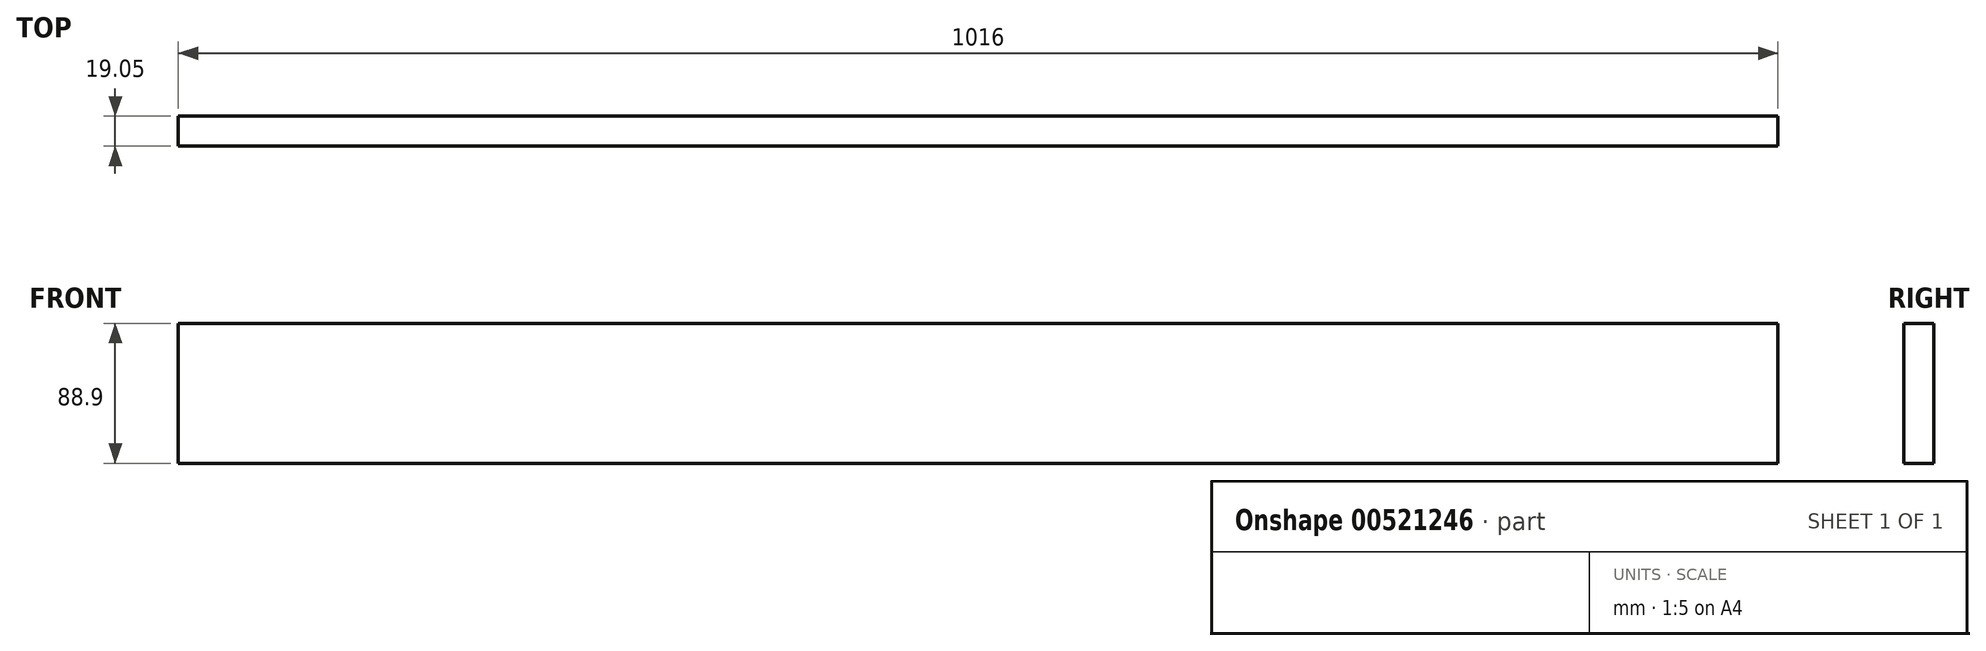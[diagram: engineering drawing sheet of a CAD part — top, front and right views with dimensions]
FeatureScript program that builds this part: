
annotation { "Feature Type Name" : "Feature", "Feature Type Description" : "" }
export const myFeature = defineFeature(function(context is Context, id is Id, definition is map)
    precondition{}
    {
        {
            var Q0;
            Q0=qCreatedBy(makeId("Front.planeOp"),FACE);
            var sketch = newSketch(context, id + "F0", { "sketchPlane" : qUnion([Q0])});
            skLineSegment(sketch, "E0.bottom", {"start": v(-508, 88.9) * mm, "end": v(508, 88.9) * mm});
            skLineSegment(sketch, "E0.top", {"start": v(-508, 0) * mm, "end": v(508, 0) * mm});
            skLineSegment(sketch, "E0.left", {"start": v(-508, 88.9) * mm, "end": v(-508, 0) * mm});
            skLineSegment(sketch, "E0.right", {"start": v(508, 88.9) * mm, "end": v(508, 0) * mm});
            skLineSegment(sketch, "E1", {"start": v(0, 58.07) * mm, "end": v(0, -50.51) * mm});
            skSolve(sketch);
        }
        {
            var Q0;
            Q0=makeQuery(id+"F0.imprint","IMPRINT",FACE,{"disambiguationData":[TD([[makeQuery(id+"F0.imprint","IMPRINT",EDGE,{"derivedFrom":sQuery(id+"F0.wireOp",EDGE,"E0.bottom")}),-1.0]])]});
            extrude(context, id + "F1", {"entities" : qUnion([Q0]), "depth" : 19.05 * mm, "offsetDistance" : 25.4 * mm});
        }
    });
